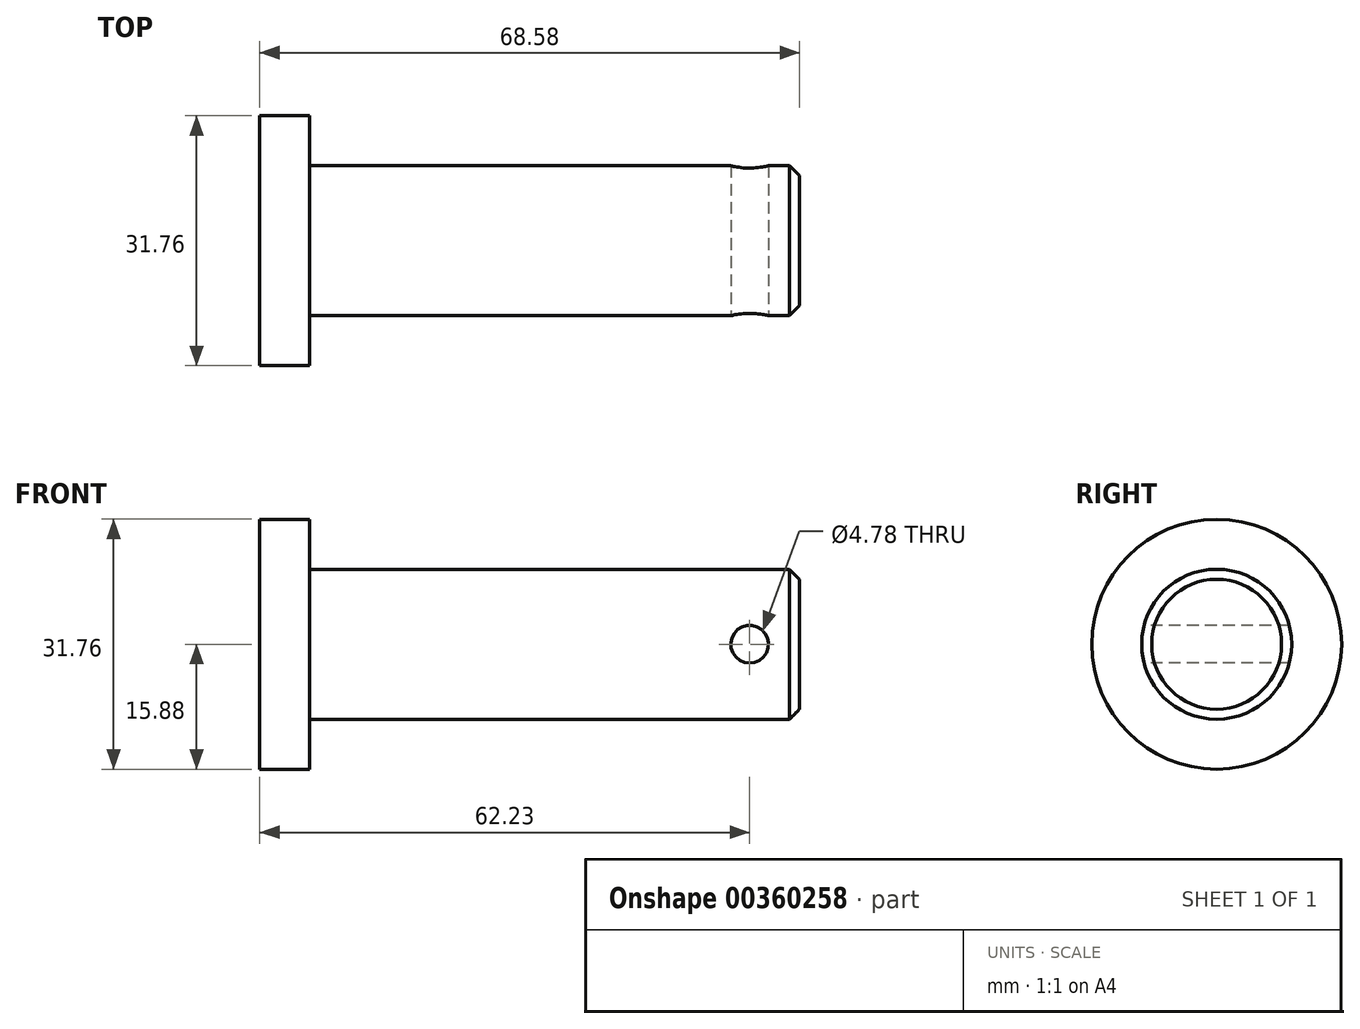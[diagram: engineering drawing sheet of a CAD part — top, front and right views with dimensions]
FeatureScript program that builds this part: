
annotation { "Feature Type Name" : "Feature", "Feature Type Description" : "" }
export const myFeature = defineFeature(function(context is Context, id is Id, definition is map)
    precondition{}
    {
        {
            var Q0;
            Q0=qCreatedBy(makeId("Front.planeOp"),FACE);
            var sketch = newSketch(context, id + "F0", { "sketchPlane" : qUnion([Q0])});
            skLineSegment(sketch, "E0", {"start": v(-63.7, 0) * mm, "end": v(0, 0) * mm, "construction": true});
            skLineSegment(sketch, "E1", {"start": v(0, 0) * mm, "end": v(0, 15.88) * mm});
            skLineSegment(sketch, "E2", {"start": v(0, 15.88) * mm, "end": v(6.35, 15.88) * mm});
            skLineSegment(sketch, "E3", {"start": v(6.35, 15.88) * mm, "end": v(6.35, 0) * mm});
            skLineSegment(sketch, "E4", {"start": v(6.35, 0) * mm, "end": v(0, 0) * mm});
            skLineSegment(sketch, "E5", {"start": v(6.35, 9.53) * mm, "end": v(68.58, 9.53) * mm});
            skLineSegment(sketch, "E6", {"start": v(68.58, 9.53) * mm, "end": v(68.58, 0) * mm});
            skLineSegment(sketch, "E7", {"start": v(6.35, 0) * mm, "end": v(68.58, 0) * mm});
            skPoint(sketch, "E8", {"position": v(37.46, 0) * mm});
            skSolve(sketch);
        }
        {
            var Q0;
            Q0=makeQuery(id+"F0.imprint","IMPRINT",FACE,{"disambiguationData":[TD([[makeQuery(id+"F0.imprint","IMPRINT",EDGE,{"derivedFrom":sQuery(id+"F0.wireOp",EDGE,"E1")}),-1.0]])]});
            var Q1;
            {var subQ2=sQuery(id+"F0.wireOp",EDGE,"E5");Q1=makeQuery(id+"F0.imprint","IMPRINT",FACE,{"disambiguationData":[TD([[makeQuery(id+"F0.imprint","IMPRINT",EDGE,{"derivedFrom":subQ2}),-1.0]])]});}
            var Q2;
            Q2=sQuery(id+"F0.wireOp",EDGE,"E7");
            revolve(context, id + "F1", {"entities" : qUnion([Q0, Q1]), "axis" : qUnion([Q2]), "revolveType" : RevolveType.FULL});
        }
        {
            var Q0;
            Q0=makeQuery(id+"F1.opRevolve","SWEPT_EDGE",EDGE,{"disambiguationData":[OSD([sQuery(id+"F0.wireOp",EDGE,"E5"),sQuery(id+"F0.wireOp",EDGE,"E6")])]});
            chamfer(context, id + "F2", {"entities" : qUnion([Q0]), "chamferType" : ChamferType.OFFSET_ANGLE, "width" : 1.27 * mm, "oppositeDirection" : false, "angle" : 45 * degree, "tangentPropagation" : true});
        }
        {
            var Q0;
            Q0=qCreatedBy(makeId("Front.planeOp"),FACE);
            var sketch = newSketch(context, id + "F3", { "sketchPlane" : qUnion([Q0])});
            skCircle(sketch, "E9", {"center": v(62.23, 0) * mm, "radius": 2.39 * mm});
            skSolve(sketch);
        }
        {
            var Q0;
            Q0 = qSketchRegion(id + "F3", true);
            extrude(context, id + "F4", {"entities" : qUnion([Q0]), "operationType" : NewBodyOperationType.REMOVE, "endBound" : BoundingType.THROUGH_ALL, "oppositeDirection" : true, "depth" : 25.4 * mm, "hasSecondDirection" : true, "secondDirectionBound" : SecondDirectionBoundingType.THROUGH_ALL, "secondDirectionOppositeDirection" : false, "secondDirectionDepth" : 25.4 * mm});
        }
    });
